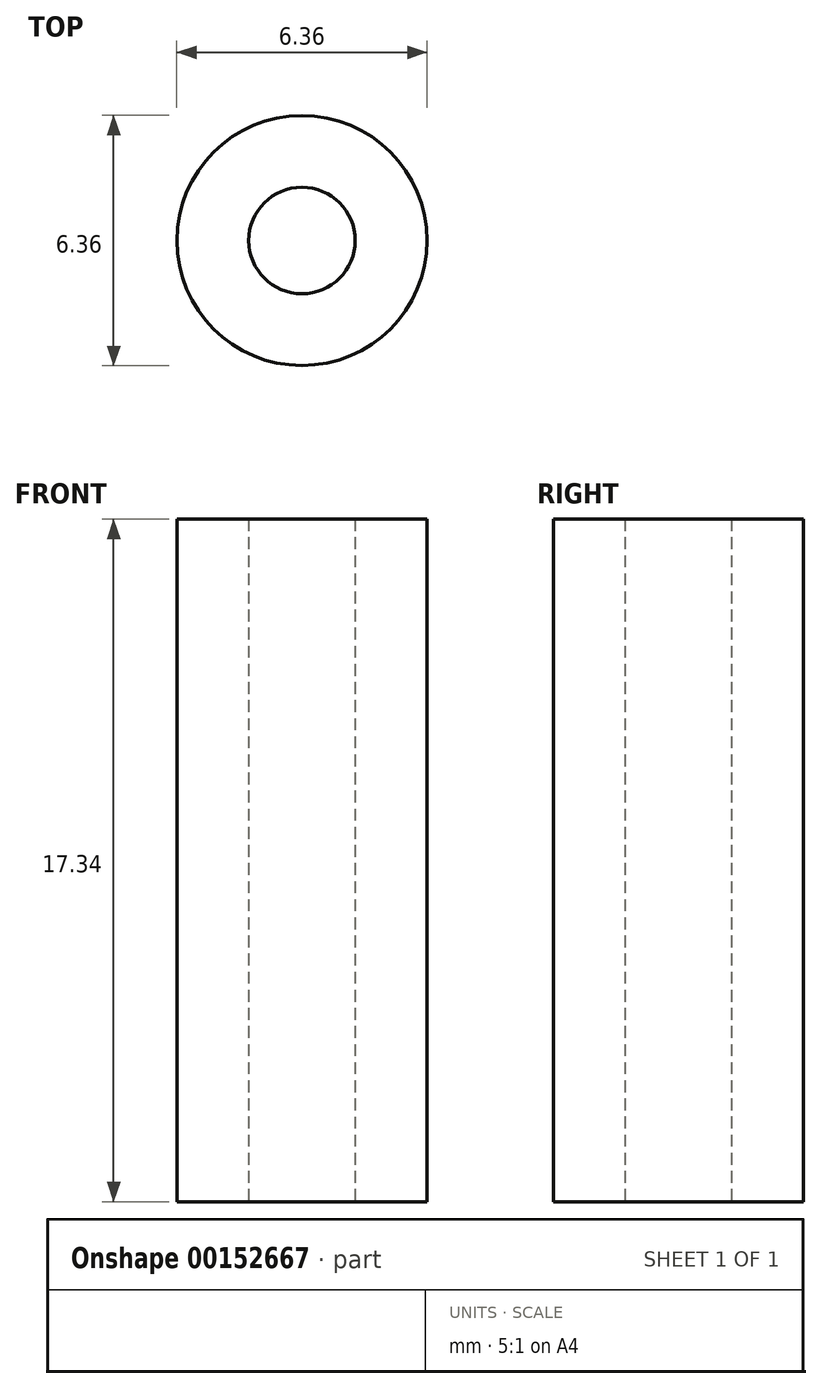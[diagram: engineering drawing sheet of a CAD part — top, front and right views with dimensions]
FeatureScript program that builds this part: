
annotation { "Feature Type Name" : "Feature", "Feature Type Description" : "" }
export const myFeature = defineFeature(function(context is Context, id is Id, definition is map)
    precondition{}
    {
        {
            var Q0;
            Q0=qCreatedBy(makeId("Top.planeOp"),FACE);
            var sketch = newSketch(context, id + "F0", { "sketchPlane" : qUnion([Q0])});
            skCircle(sketch, "E0", {"center": v(0, 0) * mm, "radius": 3.18 * mm});
            skCircle(sketch, "E1", {"center": v(0, 0) * mm, "radius": 1.35 * mm});
            skSolve(sketch);
        }
        {
            var Q0;
            Q0 = qSketchRegion(id + "F0", true);
            extrude(context, id + "F1", {"entities" : qUnion([Q0]), "depth" : 17.34 * mm});
        }
    });
